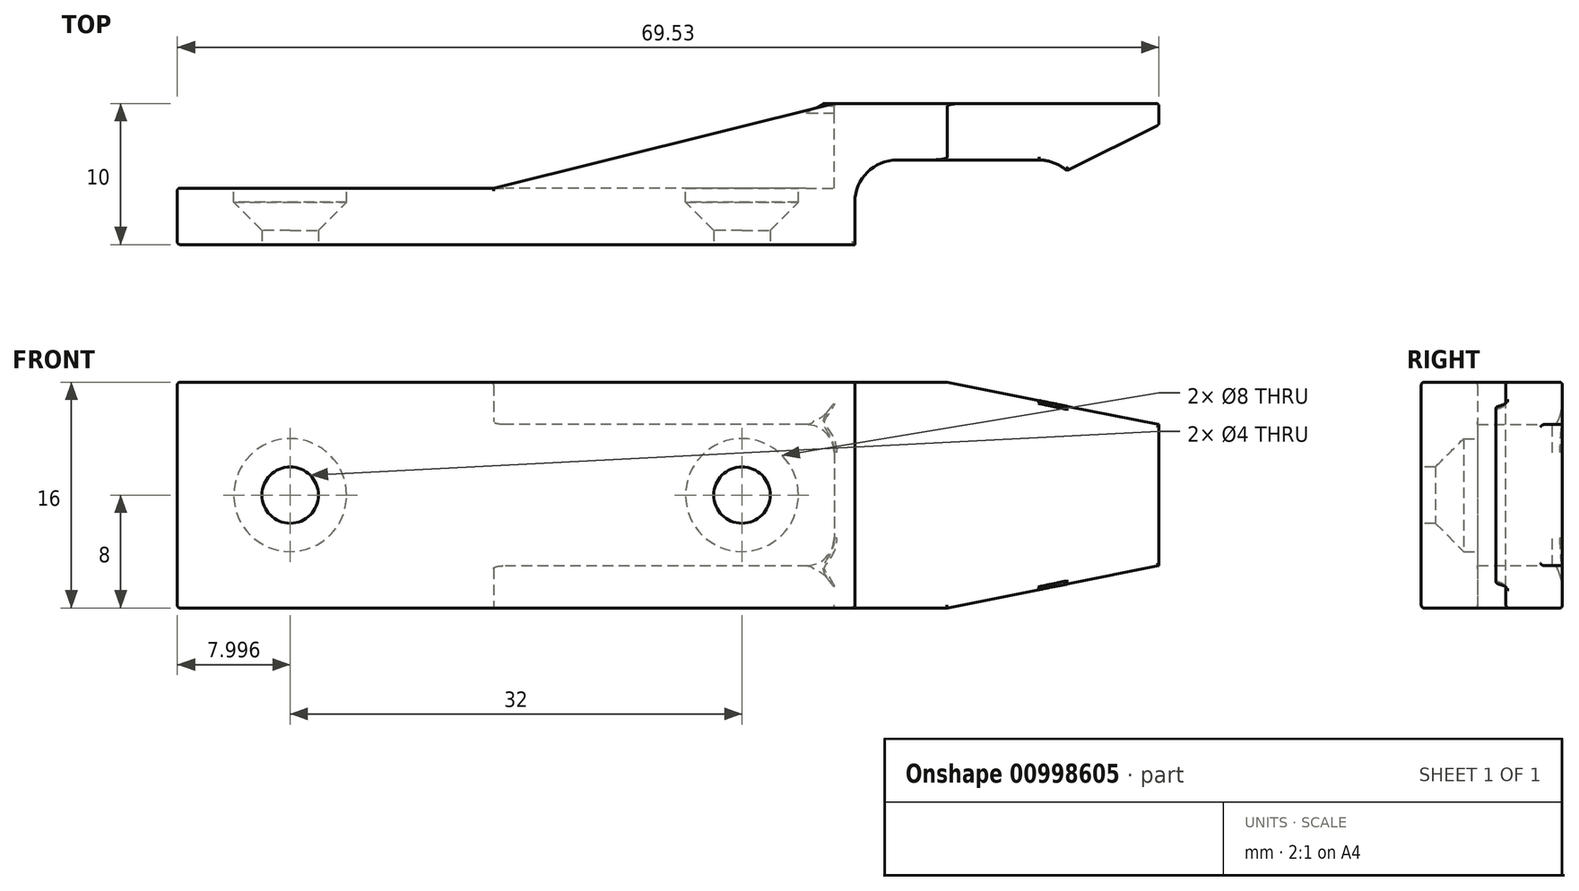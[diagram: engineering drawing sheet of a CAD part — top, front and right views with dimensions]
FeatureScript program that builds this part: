
annotation { "Feature Type Name" : "Feature", "Feature Type Description" : "" }
export const myFeature = defineFeature(function(context is Context, id is Id, definition is map)
    precondition{}
    {
        {
            var Q0;
            Q0=qCreatedBy(makeId("Top.planeOp"),FACE);
            var sketch = newSketch(context, id + "F0", { "sketchPlane" : qUnion([Q0])});
            skLineSegment(sketch, "E0", {"start": v(-63.96, -16.94) * mm, "end": v(-1.46, -16.94) * mm});
            skLineSegment(sketch, "E1", {"start": v(-1.46, -16.94) * mm, "end": v(-1.46, -11.94) * mm});
            skLineSegment(sketch, "E2", {"start": v(-1.46, -11.94) * mm, "end": v(5.57, -8.44) * mm});
            skLineSegment(sketch, "E3", {"start": v(5.57, -8.44) * mm, "end": v(5.57, -6.94) * mm});
            skLineSegment(sketch, "E4", {"start": v(5.57, -6.94) * mm, "end": v(-17.43, -6.94) * mm});
            skLineSegment(sketch, "E5", {"start": v(-17.43, -6.94) * mm, "end": v(-41.56, -12.94) * mm});
            skLineSegment(sketch, "E6", {"start": v(-63.96, -16.94) * mm, "end": v(-63.96, -12.94) * mm});
            skLineSegment(sketch, "E7", {"start": v(-63.96, -12.94) * mm, "end": v(-41.56, -12.94) * mm});
            skSolve(sketch);
        }
        {
            var Q0;
            Q0 = qSketchRegion(id + "F0", true);
            extrude(context, id + "F1", {"entities" : qUnion([Q0]), "depth" : 16 * mm, "offsetDistance" : 25 * mm});
        }
        {
            var Q0;
            Q0=makeQuery(id+"F1.opExtrude","CAP_FACE",FACE,{"disambiguationData":[OSD([sQuery(id+"F0.wireOp",EDGE,"E0"),sQuery(id+"F0.wireOp",EDGE,"E1"),sQuery(id+"F0.wireOp",EDGE,"E2"),sQuery(id+"F0.wireOp",EDGE,"E3"),sQuery(id+"F0.wireOp",EDGE,"E4"),sQuery(id+"F0.wireOp",EDGE,"E5"),sQuery(id+"F0.wireOp",EDGE,"E6"),sQuery(id+"F0.wireOp",EDGE,"E7")])],"isStart":false});
            var sketch = newSketch(context, id + "F2", { "sketchPlane" : qUnion([Q0])});
            skLineSegment(sketch, "E8", {"start": v(0.04, -16.94) * mm, "end": v(-15.96, -16.94) * mm});
            skPoint(sketch, "E9", {"position": v(-15.96, -13.94) * mm});
            skPoint(sketch, "E10", {"position": v(0.04, -13.94) * mm});
            skPoint(sketch, "E11", {"position": v(-2.96, -13.94) * mm});
            skPoint(sketch, "E12", {"position": v(-12.96, -13.94) * mm});
            skPoint(sketch, "E13", {"position": v(-12.96, -10.94) * mm});
            skArc(sketch, "E14", {"start": v(-12.96, -10.94) * mm, "mid": v(-15.08, -11.81) * mm, "end": v(-15.96, -13.94) * mm});
            skArc(sketch, "E15", {"start": v(-2.96, -10.94) * mm, "mid": v(-0.84, -11.81) * mm, "end": v(0.04, -13.94) * mm});
            skLineSegment(sketch, "E16", {"start": v(0.04, -13.94) * mm, "end": v(0.04, -16.94) * mm});
            skLineSegment(sketch, "E17", {"start": v(-15.96, -16.94) * mm, "end": v(0.04, -16.94) * mm});
            skLineSegment(sketch, "E18", {"start": v(-15.96, -16.94) * mm, "end": v(-15.96, -13.94) * mm});
            skLineSegment(sketch, "E19", {"start": v(-12.96, -10.94) * mm, "end": v(-2.96, -10.94) * mm});
            skSolve(sketch);
        }
        {
            var Q0;
            Q0 = qSketchRegion(id + "F2", true);
            extrude(context, id + "F3", {"entities" : qUnion([Q0]), "operationType" : NewBodyOperationType.REMOVE, "oppositeDirection" : true, "depth" : 25 * mm, "offsetDistance" : 25 * mm});
        }
        {
            var Q0;
            Q0=makeQuery(id+"F1.opExtrude","SWEPT_FACE",FACE,{"disambiguationData":[OSD([sQuery(id+"F0.wireOp",EDGE,"E4")])]});
            var sketch = newSketch(context, id + "F4", { "sketchPlane" : qUnion([Q0])});
            skLineSegment(sketch, "E20", {"start": v(-5.57, 13) * mm, "end": v(9.43, 16) * mm});
            skLineSegment(sketch, "E21", {"start": v(9.43, 16) * mm, "end": v(-5.57, 16) * mm});
            skLineSegment(sketch, "E22", {"start": v(-5.57, 16) * mm, "end": v(-5.57, 13) * mm});
            skLineSegment(sketch, "E23", {"start": v(-5.57, 3) * mm, "end": v(9.43, 0) * mm});
            skLineSegment(sketch, "E24", {"start": v(9.43, 0) * mm, "end": v(-5.57, 0) * mm});
            skLineSegment(sketch, "E25", {"start": v(-5.57, 0) * mm, "end": v(-5.57, 3) * mm});
            skSolve(sketch);
        }
        {
            var Q0;
            Q0 = qSketchRegion(id + "F4", true);
            extrude(context, id + "F5", {"entities" : qUnion([Q0]), "operationType" : NewBodyOperationType.REMOVE, "oppositeDirection" : true, "depth" : 25 * mm, "offsetDistance" : 25 * mm});
        }
        {
            var Q0;
            Q0=makeQuery(id+"F1.opExtrude","SWEPT_FACE",FACE,{"disambiguationData":[OSD([sQuery(id+"F0.wireOp",EDGE,"E4")])]});
            var sketch = newSketch(context, id + "F6", { "sketchPlane" : qUnion([Q0])});
            skLineSegment(sketch, "E26", {"start": v(17.43, 13) * mm, "end": v(17.43, 3) * mm});
            skLineSegment(sketch, "E27", {"start": v(41.56, 13) * mm, "end": v(41.56, 3) * mm});
            skLineSegment(sketch, "E28", {"start": v(17.43, 13) * mm, "end": v(41.56, 13) * mm});
            skLineSegment(sketch, "E29", {"start": v(41.56, 3) * mm, "end": v(17.43, 3) * mm});
            skSolve(sketch);
        }
        {
            var Q0;
            Q0 = qSketchRegion(id + "F6", true);
            extrude(context, id + "F7", {"entities" : qUnion([Q0]), "operationType" : NewBodyOperationType.REMOVE, "oppositeDirection" : true, "depth" : 6 * mm, "offsetDistance" : 25 * mm});
        }
        {
            var Q0;
            Q0=makeQuery(id+"F7.boolean.opBoolean","MERGE",FACE,{"derivedFrom":[makeQuery(id+"F1.opExtrude","SWEPT_FACE",FACE,{"disambiguationData":[OSD([sQuery(id+"F0.wireOp",EDGE,"E7")])]})],"fromTools":[makeQuery(id+"F7.opExtrude","CAP_FACE",FACE,{"disambiguationData":[OSD([sQuery(id+"F6.wireOp",EDGE,"E26"),sQuery(id+"F6.wireOp",EDGE,"E27"),sQuery(id+"F6.wireOp",EDGE,"E28"),sQuery(id+"F6.wireOp",EDGE,"E29")])],"isStart":false})]});
            var sketch = newSketch(context, id + "F8", { "sketchPlane" : qUnion([Q0])});
            skCircle(sketch, "E30", {"center": v(55.96, 8) * mm, "radius": 4 * mm});
            skCircle(sketch, "E31", {"center": v(23.96, 8) * mm, "radius": 4 * mm});
            skSolve(sketch);
        }
        {
            var Q0;
            Q0 = qSketchRegion(id + "F8", true);
            extrude(context, id + "F9", {"entities" : qUnion([Q0]), "operationType" : NewBodyOperationType.REMOVE, "oppositeDirection" : true, "depth" : 1 * mm, "offsetDistance" : 25 * mm});
        }
        {
            var Q0;
            Q0=makeQuery(id+"F9.boolean.opBoolean","COPY",FACE,{"derivedFrom":makeQuery(id+"F9.opExtrude","CAP_FACE",FACE,{"disambiguationData":[OSD([sQuery(id+"F8.wireOp",EDGE,"E31")])],"isStart":false})});
            var Q1;
            Q1=makeQuery(id+"F9.boolean.opBoolean","COPY",FACE,{"derivedFrom":makeQuery(id+"F9.opExtrude","CAP_FACE",FACE,{"disambiguationData":[OSD([sQuery(id+"F8.wireOp",EDGE,"E30")])],"isStart":false})});
            extrude(context, id + "F10", {"entities" : qUnion([Q0, Q1]), "operationType" : NewBodyOperationType.REMOVE, "oppositeDirection" : true, "depth" : 25 * mm, "offsetDistance" : 25 * mm, "hasDraft" : true, "draftAngle" : 45 * degree, "draftPullDirection" : true});
        }
        {
            var Q0;
            Q0=makeQuery(id+"F1.opExtrude","SWEPT_FACE",FACE,{"disambiguationData":[OSD([sQuery(id+"F0.wireOp",EDGE,"E0")])]});
            var sketch = newSketch(context, id + "F11", { "sketchPlane" : qUnion([Q0])});
            skCircle(sketch, "E32", {"center": v(-55.96, 8) * mm, "radius": 2 * mm});
            skCircle(sketch, "E33", {"center": v(-23.96, 8) * mm, "radius": 2 * mm});
            skSolve(sketch);
        }
        {
            var Q0;
            Q0 = qSketchRegion(id + "F11", true);
            extrude(context, id + "F12", {"entities" : qUnion([Q0]), "operationType" : NewBodyOperationType.REMOVE, "oppositeDirection" : true, "depth" : 25 * mm, "offsetDistance" : 25 * mm});
        }
        {
            var Q0;
            Q0=makeQuery(id+"F1.opExtrude","CAP_EDGE",EDGE,{"disambiguationData":[OSD([sQuery(id+"F0.wireOp",EDGE,"E6")])],"isStart":false});
            var Q1;
            Q1=makeQuery(id+"F1.opExtrude","CAP_EDGE",EDGE,{"disambiguationData":[OSD([sQuery(id+"F0.wireOp",EDGE,"E6")])],"isStart":true});
            var Q2;
            Q2=makeQuery(id+"F1.opExtrude","CAP_EDGE",EDGE,{"disambiguationData":[OSD([sQuery(id+"F0.wireOp",EDGE,"E7")])],"isStart":false});
            var Q3;
            Q3=makeQuery(id+"F1.opExtrude","CAP_EDGE",EDGE,{"disambiguationData":[OSD([sQuery(id+"F0.wireOp",EDGE,"E5")])],"isStart":false});
            var Q4;
            Q4=makeQuery(id+"F1.opExtrude","CAP_EDGE",EDGE,{"disambiguationData":[OSD([sQuery(id+"F0.wireOp",EDGE,"E0")])],"isStart":false});
            var Q5;
            Q5=makeQuery(id+"F3.boolean.opBoolean","COPY",EDGE,{"derivedFrom":makeQuery(id+"F3.opExtrude","CAP_EDGE",EDGE,{"disambiguationData":[OSD([sQuery(id+"F2.wireOp",EDGE,"E18")])],"isStart":true})});
            var Q6;
            Q6=makeQuery(id+"F1.opExtrude","CAP_EDGE",EDGE,{"disambiguationData":[OSD([sQuery(id+"F0.wireOp",EDGE,"E0")])],"isStart":true});
            var Q7;
            Q7=makeQuery(id+"F1.opExtrude","CAP_EDGE",EDGE,{"disambiguationData":[OSD([sQuery(id+"F0.wireOp",EDGE,"E7")])],"isStart":true});
            var Q8;
            Q8=makeQuery(id+"F1.opExtrude","CAP_EDGE",EDGE,{"disambiguationData":[OSD([sQuery(id+"F0.wireOp",EDGE,"E5")])],"isStart":true});
            var Q9;
            Q9=makeQuery(id+"F7.boolean.opBoolean","INTERSECT",EDGE,{"derivedFrom":[makeQuery(id+"F1.opExtrude","SWEPT_FACE",FACE,{"disambiguationData":[OSD([sQuery(id+"F0.wireOp",EDGE,"E5")])]}),makeQuery(id+"F7.opExtrude","SWEPT_FACE",FACE,{"disambiguationData":[OSD([sQuery(id+"F6.wireOp",EDGE,"E29")])]})]});
            var Q10;
            Q10=makeQuery(id+"F7.boolean.opBoolean","INTERSECT",EDGE,{"derivedFrom":[makeQuery(id+"F1.opExtrude","SWEPT_FACE",FACE,{"disambiguationData":[OSD([sQuery(id+"F0.wireOp",EDGE,"E5")])]}),makeQuery(id+"F7.opExtrude","SWEPT_FACE",FACE,{"disambiguationData":[OSD([sQuery(id+"F6.wireOp",EDGE,"E28")])]})]});
            var Q11;
            Q11=makeQuery(id+"F1.opExtrude","CAP_EDGE",EDGE,{"disambiguationData":[OSD([sQuery(id+"F0.wireOp",EDGE,"E4")])],"isStart":false});
            var Q12;
            Q12=makeQuery(id+"F5.boolean.opBoolean","COPY",EDGE,{"derivedFrom":makeQuery(id+"F5.opExtrude","CAP_EDGE",EDGE,{"disambiguationData":[OSD([sQuery(id+"F4.wireOp",EDGE,"E20")])],"isStart":true})});
            var Q13;
            Q13=makeQuery(id+"F1.opExtrude","SWEPT_EDGE",EDGE,{"disambiguationData":[OSD([sQuery(id+"F0.wireOp",EDGE,"E3"),sQuery(id+"F0.wireOp",EDGE,"E4")])]});
            var Q14;
            Q14=makeQuery(id+"F5.boolean.opBoolean","COPY",EDGE,{"derivedFrom":makeQuery(id+"F5.opExtrude","CAP_EDGE",EDGE,{"disambiguationData":[OSD([sQuery(id+"F4.wireOp",EDGE,"E23")])],"isStart":true})});
            var Q15;
            Q15=makeQuery(id+"F1.opExtrude","CAP_EDGE",EDGE,{"disambiguationData":[OSD([sQuery(id+"F0.wireOp",EDGE,"E4")])],"isStart":true});
            var Q16;
            Q16=makeQuery(id+"F3.boolean.opBoolean","INTERSECT",EDGE,{"derivedFrom":[makeQuery(id+"F1.opExtrude","SWEPT_FACE",FACE,{"disambiguationData":[OSD([sQuery(id+"F0.wireOp",EDGE,"E2")])]}),makeQuery(id+"F3.opExtrude","SWEPT_FACE",FACE,{"disambiguationData":[OSD([sQuery(id+"F2.wireOp",EDGE,"E15")])]})]});
            var Q17;
            Q17=makeQuery(id+"F5.boolean.opBoolean","INTERSECT",EDGE,{"derivedFrom":[makeQuery(id+"F1.opExtrude","SWEPT_FACE",FACE,{"disambiguationData":[OSD([sQuery(id+"F0.wireOp",EDGE,"E2")])]}),makeQuery(id+"F5.opExtrude","SWEPT_FACE",FACE,{"disambiguationData":[OSD([sQuery(id+"F4.wireOp",EDGE,"E23")])]})]});
            var Q18;
            Q18=makeQuery(id+"F5.boolean.opBoolean","INTERSECT",EDGE,{"derivedFrom":[makeQuery(id+"F1.opExtrude","SWEPT_FACE",FACE,{"disambiguationData":[OSD([sQuery(id+"F0.wireOp",EDGE,"E2")])]}),makeQuery(id+"F5.opExtrude","SWEPT_FACE",FACE,{"disambiguationData":[OSD([sQuery(id+"F4.wireOp",EDGE,"E20")])]})]});
            var Q19;
            Q19=makeQuery(id+"F1.opExtrude","SWEPT_EDGE",EDGE,{"disambiguationData":[OSD([sQuery(id+"F0.wireOp",EDGE,"E2"),sQuery(id+"F0.wireOp",EDGE,"E3")])]});
            var Q20;
            Q20=makeQuery(id+"F5.boolean.opBoolean","COPY",EDGE,{"derivedFrom":makeQuery(id+"F5.opExtrude","SWEPT_EDGE",EDGE,{"disambiguationData":[OSD([sQuery(id+"F0.wireOp",EDGE,"E3"),sQuery(id+"F0.wireOp",EDGE,"E4"),sQuery(id+"F4.wireOp",EDGE,"E23"),sQuery(id+"F4.wireOp",EDGE,"E25")])]})});
            var Q21;
            Q21=makeQuery(id+"F5.boolean.opBoolean","COPY",EDGE,{"derivedFrom":makeQuery(id+"F5.opExtrude","SWEPT_EDGE",EDGE,{"disambiguationData":[OSD([sQuery(id+"F0.wireOp",EDGE,"E3"),sQuery(id+"F0.wireOp",EDGE,"E4"),sQuery(id+"F4.wireOp",EDGE,"E20"),sQuery(id+"F4.wireOp",EDGE,"E22")])]})});
            var Q22;
            Q22=makeQuery(id+"F5.boolean.opBoolean","INTERSECT",EDGE,{"derivedFrom":[makeQuery(id+"F3.boolean.opBoolean","COPY",FACE,{"derivedFrom":makeQuery(id+"F3.opExtrude","SWEPT_FACE",FACE,{"disambiguationData":[OSD([sQuery(id+"F2.wireOp",EDGE,"E15")])]})}),makeQuery(id+"F5.opExtrude","SWEPT_FACE",FACE,{"disambiguationData":[OSD([sQuery(id+"F4.wireOp",EDGE,"E20")])]})]});
            var Q23;
            Q23=makeQuery(id+"F5.boolean.opBoolean","INTERSECT",EDGE,{"derivedFrom":[makeQuery(id+"F3.boolean.opBoolean","COPY",FACE,{"derivedFrom":makeQuery(id+"F3.opExtrude","SWEPT_FACE",FACE,{"disambiguationData":[OSD([sQuery(id+"F2.wireOp",EDGE,"E19")])]})}),makeQuery(id+"F5.opExtrude","SWEPT_FACE",FACE,{"disambiguationData":[OSD([sQuery(id+"F4.wireOp",EDGE,"E20")])]})]});
            var Q24;
            Q24=makeQuery(id+"F3.boolean.opBoolean","COPY",EDGE,{"derivedFrom":makeQuery(id+"F3.opExtrude","CAP_EDGE",EDGE,{"disambiguationData":[OSD([sQuery(id+"F2.wireOp",EDGE,"E19")])],"isStart":true})});
            var Q25;
            Q25=makeQuery(id+"F3.boolean.opBoolean","COPY",EDGE,{"derivedFrom":makeQuery(id+"F3.opExtrude","CAP_EDGE",EDGE,{"disambiguationData":[OSD([sQuery(id+"F2.wireOp",EDGE,"E14")])],"isStart":true})});
            var Q26;
            Q26=makeQuery(id+"F5.boolean.opBoolean","INTERSECT",EDGE,{"derivedFrom":[makeQuery(id+"F3.boolean.opBoolean","COPY",FACE,{"derivedFrom":makeQuery(id+"F3.opExtrude","SWEPT_FACE",FACE,{"disambiguationData":[OSD([sQuery(id+"F2.wireOp",EDGE,"E15")])]})}),makeQuery(id+"F5.opExtrude","SWEPT_FACE",FACE,{"disambiguationData":[OSD([sQuery(id+"F4.wireOp",EDGE,"E23")])]})]});
            var Q27;
            Q27=makeQuery(id+"F5.boolean.opBoolean","INTERSECT",EDGE,{"derivedFrom":[makeQuery(id+"F3.boolean.opBoolean","COPY",FACE,{"derivedFrom":makeQuery(id+"F3.opExtrude","SWEPT_FACE",FACE,{"disambiguationData":[OSD([sQuery(id+"F2.wireOp",EDGE,"E19")])]})}),makeQuery(id+"F5.opExtrude","SWEPT_FACE",FACE,{"disambiguationData":[OSD([sQuery(id+"F4.wireOp",EDGE,"E23")])]})]});
            var Q28;
            Q28=makeQuery(id+"F3.boolean.opBoolean","INTERSECT",EDGE,{"derivedFrom":[makeQuery(id+"F1.opExtrude","CAP_FACE",FACE,{"disambiguationData":[OSD([sQuery(id+"F0.wireOp",EDGE,"E0"),sQuery(id+"F0.wireOp",EDGE,"E1"),sQuery(id+"F0.wireOp",EDGE,"E2"),sQuery(id+"F0.wireOp",EDGE,"E3"),sQuery(id+"F0.wireOp",EDGE,"E4"),sQuery(id+"F0.wireOp",EDGE,"E5"),sQuery(id+"F0.wireOp",EDGE,"E6"),sQuery(id+"F0.wireOp",EDGE,"E7")])],"isStart":true}),makeQuery(id+"F3.opExtrude","SWEPT_FACE",FACE,{"disambiguationData":[OSD([sQuery(id+"F2.wireOp",EDGE,"E19")])]})]});
            var Q29;
            Q29=makeQuery(id+"F3.boolean.opBoolean","INTERSECT",EDGE,{"derivedFrom":[makeQuery(id+"F1.opExtrude","CAP_FACE",FACE,{"disambiguationData":[OSD([sQuery(id+"F0.wireOp",EDGE,"E0"),sQuery(id+"F0.wireOp",EDGE,"E1"),sQuery(id+"F0.wireOp",EDGE,"E2"),sQuery(id+"F0.wireOp",EDGE,"E3"),sQuery(id+"F0.wireOp",EDGE,"E4"),sQuery(id+"F0.wireOp",EDGE,"E5"),sQuery(id+"F0.wireOp",EDGE,"E6"),sQuery(id+"F0.wireOp",EDGE,"E7")])],"isStart":true}),makeQuery(id+"F3.opExtrude","SWEPT_FACE",FACE,{"disambiguationData":[OSD([sQuery(id+"F2.wireOp",EDGE,"E14")])]})]});
            var Q30;
            Q30=makeQuery(id+"F3.boolean.opBoolean","INTERSECT",EDGE,{"derivedFrom":[makeQuery(id+"F1.opExtrude","CAP_FACE",FACE,{"disambiguationData":[OSD([sQuery(id+"F0.wireOp",EDGE,"E0"),sQuery(id+"F0.wireOp",EDGE,"E1"),sQuery(id+"F0.wireOp",EDGE,"E2"),sQuery(id+"F0.wireOp",EDGE,"E3"),sQuery(id+"F0.wireOp",EDGE,"E4"),sQuery(id+"F0.wireOp",EDGE,"E5"),sQuery(id+"F0.wireOp",EDGE,"E6"),sQuery(id+"F0.wireOp",EDGE,"E7")])],"isStart":true}),makeQuery(id+"F3.opExtrude","SWEPT_FACE",FACE,{"disambiguationData":[OSD([sQuery(id+"F2.wireOp",EDGE,"E18")])]})]});
            var Q31;
            Q31=makeQuery(id+"F3.boolean.opBoolean","COPY",EDGE,{"derivedFrom":makeQuery(id+"F3.opExtrude","SWEPT_EDGE",EDGE,{"disambiguationData":[OSD([sQuery(id+"F0.wireOp",EDGE,"E0"),sQuery(id+"F2.wireOp",EDGE,"E17"),sQuery(id+"F2.wireOp",EDGE,"E18")])]})});
            var Q32;
            Q32=makeQuery(id+"F1.opExtrude","SWEPT_EDGE",EDGE,{"disambiguationData":[OSD([sQuery(id+"F0.wireOp",EDGE,"E0"),sQuery(id+"F0.wireOp",EDGE,"E6")])]});
            var Q33;
            Q33=makeQuery(id+"F1.opExtrude","SWEPT_EDGE",EDGE,{"disambiguationData":[OSD([sQuery(id+"F0.wireOp",EDGE,"E6"),sQuery(id+"F0.wireOp",EDGE,"E7")])]});
            fillet(context, id + "F13", {"entities" : qUnion([Q0, Q1, Q2, Q3, Q4, Q5, Q6, Q7, Q8, Q9, Q10, Q11, Q12, Q13, Q14, Q15, Q16, Q17, Q18, Q19, Q20, Q21, Q22, Q23, Q24, Q25, Q26, Q27, Q28, Q29, Q30, Q31, Q32, Q33]), "radius" : 0.2 * mm, "tangentPropagation" : true, "allowEdgeOverflow" : false});
        }
        {
            var Q0;
            Q0=makeQuery(id+"F7.boolean.opBoolean","COPY",EDGE,{"derivedFrom":makeQuery(id+"F7.opExtrude","SWEPT_EDGE",EDGE,{"disambiguationData":[OSD([sQuery(id+"F0.wireOp",EDGE,"E4"),sQuery(id+"F0.wireOp",EDGE,"E5"),sQuery(id+"F6.wireOp",EDGE,"E26"),sQuery(id+"F6.wireOp",EDGE,"E29")])]})});
            var Q1;
            Q1=makeQuery(id+"F7.boolean.opBoolean","COPY",EDGE,{"derivedFrom":makeQuery(id+"F7.opExtrude","SWEPT_EDGE",EDGE,{"disambiguationData":[OSD([sQuery(id+"F0.wireOp",EDGE,"E4"),sQuery(id+"F0.wireOp",EDGE,"E5"),sQuery(id+"F6.wireOp",EDGE,"E26"),sQuery(id+"F6.wireOp",EDGE,"E28")])]})});
            fillet(context, id + "F14", {"entities" : qUnion([Q0, Q1]), "radius" : 2 * mm, "tangentPropagation" : true, "allowEdgeOverflow" : false});
        }
        {
            var Q0;
            Q0=makeQuery(id+"F7.boolean.opBoolean","MERGE",EDGE,{"derivedFrom":[makeQuery(id+"F1.opExtrude","SWEPT_EDGE",EDGE,{"disambiguationData":[OSD([sQuery(id+"F0.wireOp",EDGE,"E4"),sQuery(id+"F0.wireOp",EDGE,"E5")])]})],"fromTools":[makeQuery(id+"F7.opExtrude","CAP_EDGE",EDGE,{"disambiguationData":[OSD([sQuery(id+"F6.wireOp",EDGE,"E26")])],"isStart":true})]});
            fillet(context, id + "F15", {"entities" : qUnion([Q0]), "radius" : 0.2 * mm, "tangentPropagation" : true, "allowEdgeOverflow" : false});
        }
    });
